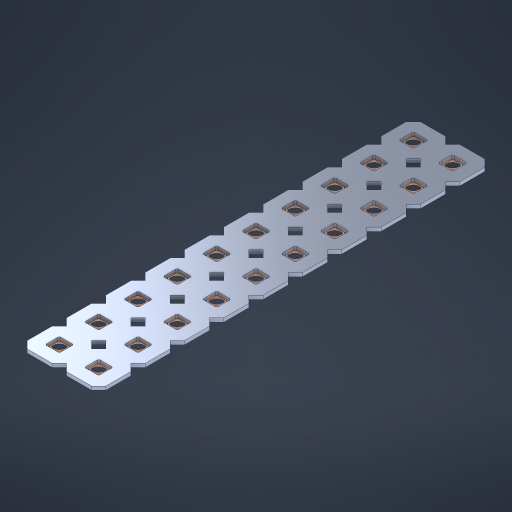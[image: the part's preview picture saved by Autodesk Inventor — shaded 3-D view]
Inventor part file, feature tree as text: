
AUTODESK INVENTOR PART (.ipt)
format: ipt  version: 2023 (Build 270158000, 158)  size: 481,280 bytes
history: native  units: in
note: dims shown in document units (in); Inventor stores cm internally (conversion verified against a paired STEP export)
features: other x21, extrude x19, sketch x2, pattern_linear x1
ambient origin geometry x8: Origin, YZ Plane, XZ Plane, XY Plane, X Axis, Y Axis, Z Axis, Center Point
bodies: Solid1 (feature_tree), Body (feature_tree)
feature tree (43):
  pattern_linear  "Rectangular Pattern1"  Spacing1=0.09in  [1 undecoded]
  sketch  "Sketch1"  dims[d1=0.5in]
  sketch  "Sketch2"  dims[d2=0.182in d3=0.09in d4=0.09in d5=0.09in d6=0.09in d7=0.09in d8=0.09in d9=0.09in d10=0.09in d11=0.02in d13=0.0in d14=0.172in d15=0.0625in d16=0.0in d19=0.5in d22=0.5in]
  other  "Srf1"
  other  "Srf126"
  other  "Srf127"
  other  "Srf128"
  other  "Srf129"
  other  "Srf130"
  other  "Srf131"
  other  "Srf250"
  other  "Srf251"
  other  "Srf252"
  other  "Srf268"
  other  "Srf269"
  other  "Srf270"
  other  "Srf271"
  other  "Srf272"
  other  "Srf273"
  other  "Srf274"
  other  "Srf275"
  other  "Srf276"
  other  "Srf277"
  other  "Circle"
  extrude  "ExtrusionSrf126"  Depth=0.09in
  extrude  "ExtrusionSrf127"  Depth=0.09in
  extrude  "ExtrusionSrf128"  Depth=0.09in
  extrude  "ExtrusionSrf129"  Depth=0.09in
  extrude  "ExtrusionSrf130"  Depth=0.09in
  extrude  "ExtrusionSrf131"  Depth=0.09in
  extrude  "ExtrusionSrf250"  Depth=0.09in
  extrude  "ExtrusionSrf251"  Depth=0.02in
  extrude  "ExtrusionSrf252"  TaperAngle=0.0deg  [1 undecoded]
  extrude  "ExtrusionSrf268"  Depth=0.5in
  extrude  "ExtrusionSrf269"  Depth=0.5in TaperAngle=0.0deg
  extrude  "ExtrusionSrf270"  Depth=0.5in
  extrude  "ExtrusionSrf271"  Depth=0.5in
  extrude  "ExtrusionSrf272"  [1 undecoded]
  extrude  "ExtrusionSrf273"  [1 undecoded]
  extrude  "ExtrusionSrf274"  [1 undecoded]
  extrude  "ExtrusionSrf275"  [1 undecoded]
  extrude  "ExtrusionSrf276"  [1 undecoded]
  extrude  "ExtrusionSrf277"  [1 undecoded]
note: 8 required parameter values undecoded (feature->parameter linkage not recoverable at this tier; creation-order binding heuristic only, values carry confidence <= 0.55)
